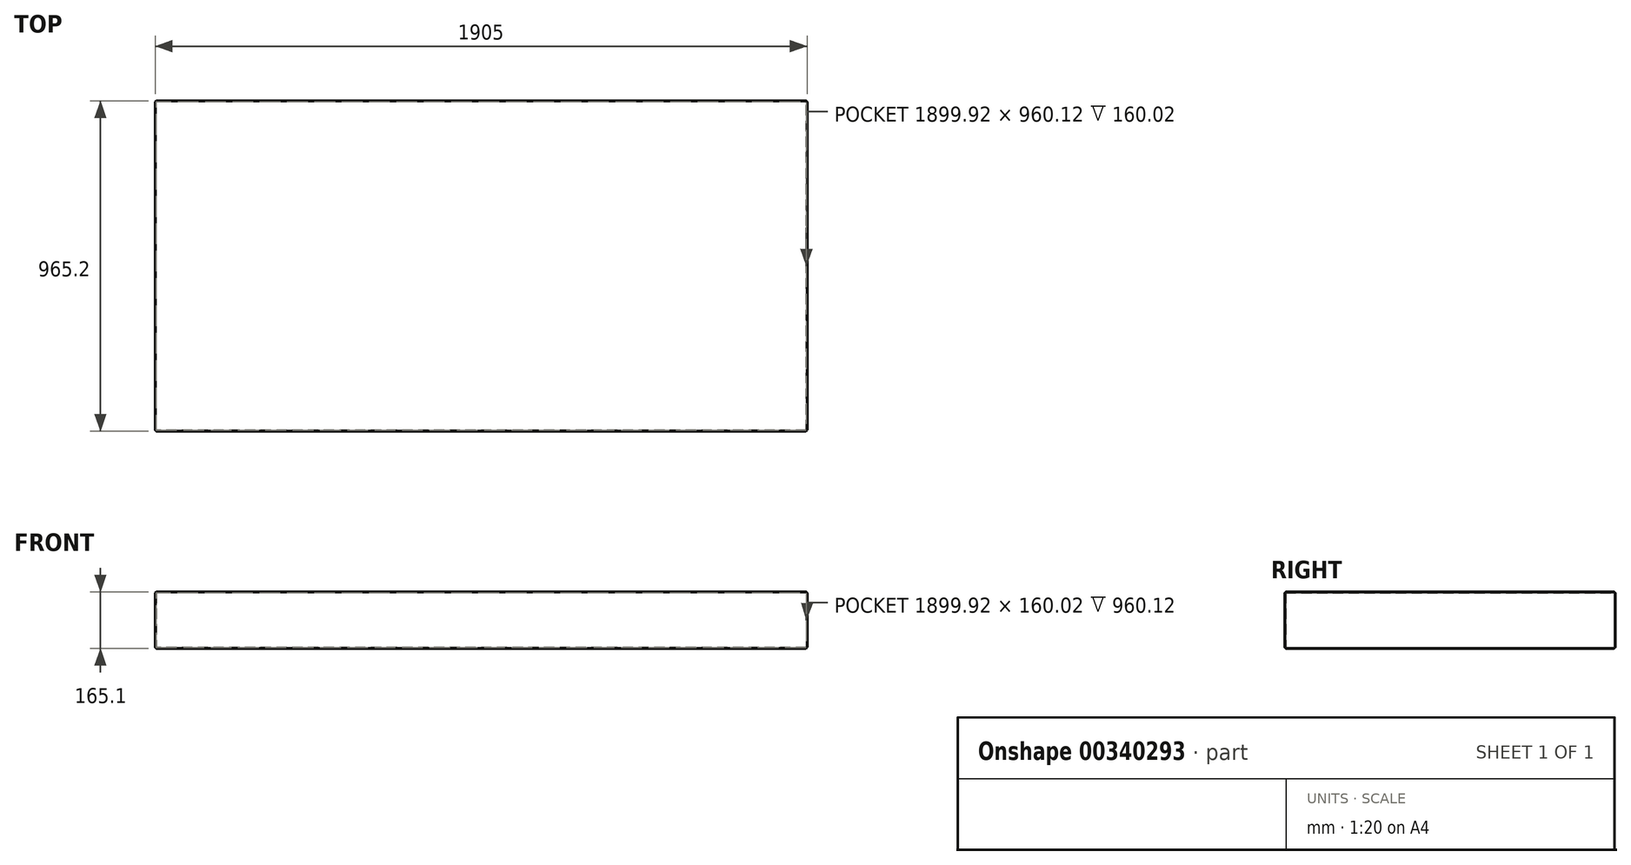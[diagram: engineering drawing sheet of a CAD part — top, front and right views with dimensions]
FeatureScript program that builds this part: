
annotation { "Feature Type Name" : "Feature", "Feature Type Description" : "" }
export const myFeature = defineFeature(function(context is Context, id is Id, definition is map)
    precondition{}
    {
        {
            var Q0;
            Q0=qCreatedBy(makeId("Top.planeOp"),FACE);
            var sketch = newSketch(context, id + "F0", { "sketchPlane" : qUnion([Q0])});
            skLineSegment(sketch, "E0.bottom", {"start": v(952.5, -482.6) * mm, "end": v(-952.5, -482.6) * mm});
            skLineSegment(sketch, "E0.top", {"start": v(952.5, 482.6) * mm, "end": v(-952.5, 482.6) * mm});
            skLineSegment(sketch, "E0.left", {"start": v(952.5, -482.6) * mm, "end": v(952.5, 482.6) * mm});
            skLineSegment(sketch, "E0.right", {"start": v(-952.5, -482.6) * mm, "end": v(-952.5, 482.6) * mm});
            skPoint(sketch, "E0.middle", {"position": v(0, 0) * mm});
            skSolve(sketch);
        }
        {
            var Q0;
            Q0 = qSketchRegion(id + "F0", true);
            extrude(context, id + "F1", {"entities" : qUnion([Q0]), "depth" : 165.1 * mm});
        }
        {
            var Q0;
            Q0=makeQuery(id+"F1.opExtrude","SWEPT_FACE",FACE,{"disambiguationData":[OSD([sQuery(id+"F0.wireOp",EDGE,"E0.bottom")])]});
            var Q1;
            Q1=makeQuery(id+"F1.opExtrude","CAP_FACE",FACE,{"disambiguationData":[OSD([sQuery(id+"F0.wireOp",EDGE,"E0.bottom"),sQuery(id+"F0.wireOp",EDGE,"E0.top"),sQuery(id+"F0.wireOp",EDGE,"E0.left"),sQuery(id+"F0.wireOp",EDGE,"E0.right")])],"isStart":false});
            var Q2;
            Q2=makeQuery(id+"F1.opExtrude","SWEPT_BODY",BODY,{"disambiguationData":[OSD([sQuery(id+"F0.wireOp",EDGE,"E0.bottom"),sQuery(id+"F0.wireOp",EDGE,"E0.top"),sQuery(id+"F0.wireOp",EDGE,"E0.left"),sQuery(id+"F0.wireOp",EDGE,"E0.right")])]});
            shell(context, id + "F2", {"isHollow" : true, "entities" : qUnion([Q0, Q1]), "parts" : qUnion([Q2]), "thickness" : 2.54 * mm});
        }
        {
            var Q0;
            Q0=makeQuery(id+"F1.opExtrude","SWEPT_FACE",FACE,{"disambiguationData":[OSD([sQuery(id+"F0.wireOp",EDGE,"E0.bottom")])]});
            var Q1;
            Q1=makeQuery(id+"F1.opExtrude","SWEPT_FACE",FACE,{"disambiguationData":[OSD([sQuery(id+"F0.wireOp",EDGE,"E0.right")])]});
            var Q2;
            Q2=makeQuery(id+"F1.opExtrude","CAP_FACE",FACE,{"disambiguationData":[OSD([sQuery(id+"F0.wireOp",EDGE,"E0.bottom"),sQuery(id+"F0.wireOp",EDGE,"E0.top"),sQuery(id+"F0.wireOp",EDGE,"E0.left"),sQuery(id+"F0.wireOp",EDGE,"E0.right")])],"isStart":false});
            var Q3;
            Q3=makeQuery(id+"F1.opExtrude","CAP_FACE",FACE,{"disambiguationData":[OSD([sQuery(id+"F0.wireOp",EDGE,"E0.bottom"),sQuery(id+"F0.wireOp",EDGE,"E0.top"),sQuery(id+"F0.wireOp",EDGE,"E0.left"),sQuery(id+"F0.wireOp",EDGE,"E0.right")])],"isStart":true});
            var Q4;
            Q4=makeQuery(id+"F1.opExtrude","SWEPT_FACE",FACE,{"disambiguationData":[OSD([sQuery(id+"F0.wireOp",EDGE,"E0.top")])]});
            var Q5;
            Q5=makeQuery(id+"F1.opExtrude","SWEPT_FACE",FACE,{"disambiguationData":[OSD([sQuery(id+"F0.wireOp",EDGE,"E0.left")])]});
            fillet(context, id + "F3", {"entities" : qUnion([Q0, Q1, Q2, Q3, Q4, Q5]), "radius" : 5.08 * mm, "tangentPropagation" : true, "allowEdgeOverflow" : false});
        }
    });
